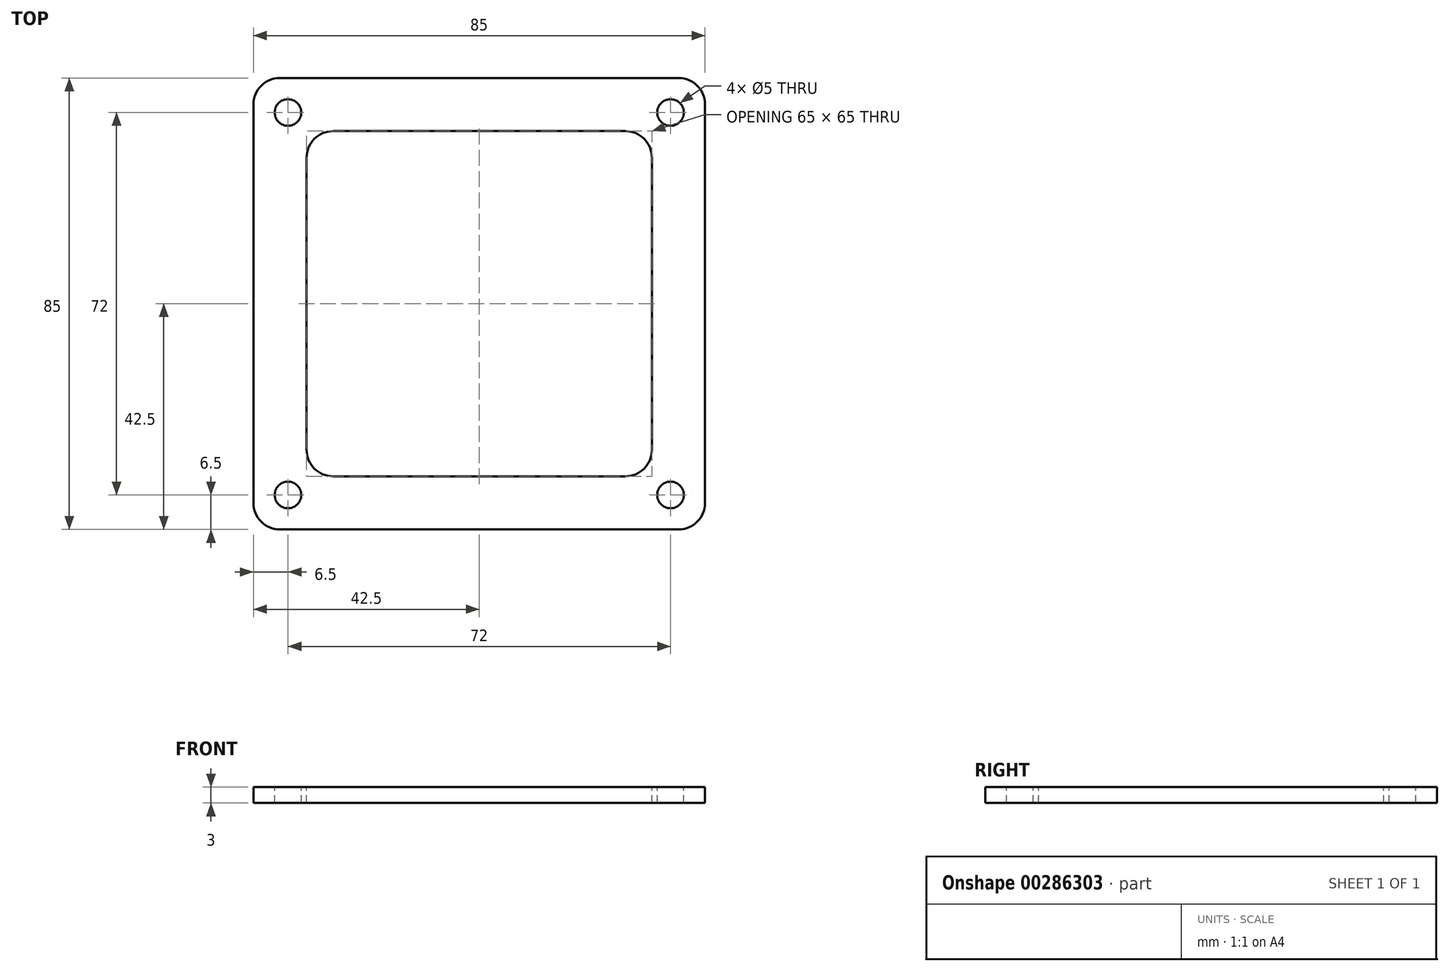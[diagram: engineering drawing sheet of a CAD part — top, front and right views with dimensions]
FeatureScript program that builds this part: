
annotation { "Feature Type Name" : "Feature", "Feature Type Description" : "" }
export const myFeature = defineFeature(function(context is Context, id is Id, definition is map)
    precondition{}
    {
        {
            var Q0;
            Q0=qCreatedBy(makeId("Top.planeOp"),FACE);
            var sketch = newSketch(context, id + "F0", { "sketchPlane" : qUnion([Q0])});
            skLineSegment(sketch, "E0.bottom", {"start": v(5, 0) * mm, "end": v(80, 0) * mm});
            skLineSegment(sketch, "E0.top", {"start": v(5, 85) * mm, "end": v(80, 85) * mm});
            skLineSegment(sketch, "E0.left", {"start": v(0, 5) * mm, "end": v(0, 80) * mm});
            skLineSegment(sketch, "E0.right", {"start": v(85, 5) * mm, "end": v(85, 80) * mm});
            skPoint(sketch, "E1.visualSharp", {"position": v(0, 0) * mm});
            skArc(sketch, "E1.filletArc", {"start": v(0, 5) * mm, "mid": v(1.46, 1.46) * mm, "end": v(5, 0) * mm});
            skPoint(sketch, "E2.visualSharp", {"position": v(0, 85) * mm});
            skArc(sketch, "E2.filletArc", {"start": v(5, 85) * mm, "mid": v(1.46, 83.54) * mm, "end": v(0, 80) * mm});
            skPoint(sketch, "E3.visualSharp", {"position": v(85, 85) * mm});
            skArc(sketch, "E3.filletArc", {"start": v(85, 80) * mm, "mid": v(83.54, 83.54) * mm, "end": v(80, 85) * mm});
            skPoint(sketch, "E4.visualSharp", {"position": v(85, 0) * mm});
            skArc(sketch, "E4.filletArc", {"start": v(80, 0) * mm, "mid": v(83.54, 1.46) * mm, "end": v(85, 5) * mm});
            skSolve(sketch);
        }
        {
            var Q0;
            Q0 = qSketchRegion(id + "F0", true);
            extrude(context, id + "F1", {"entities" : qUnion([Q0]), "depth" : 3 * mm});
        }
        {
            var Q0;
            Q0=makeQuery(id+"F1.opExtrude","CAP_FACE",FACE,{"disambiguationData":[OSD([sQuery(id+"F0.wireOp",EDGE,"E0.bottom"),sQuery(id+"F0.wireOp",EDGE,"E0.top"),sQuery(id+"F0.wireOp",EDGE,"E0.left"),sQuery(id+"F0.wireOp",EDGE,"E0.right")])],"isStart":false});
            var sketch = newSketch(context, id + "F2", { "sketchPlane" : qUnion([Q0])});
            skCircle(sketch, "E5", {"center": v(6.5, 6.5) * mm, "radius": 2.5 * mm});
            skCircle(sketch, "E6.0.1.0", {"center": v(6.5, 78.5) * mm, "radius": 2.5 * mm});
            skCircle(sketch, "E6.1.0.0", {"center": v(78.5, 6.5) * mm, "radius": 2.5 * mm});
            skCircle(sketch, "E6.1.1.0", {"center": v(78.5, 78.5) * mm, "radius": 2.5 * mm});
            skLineSegment(sketch, "E6.direction1", {"start": v(6.5, 6.5) * mm, "end": v(78.5, 6.5) * mm, "construction": true});
            skLineSegment(sketch, "E6.direction2", {"start": v(6.5, 6.5) * mm, "end": v(6.5, 78.5) * mm, "construction": true});
            skLineSegment(sketch, "E7.bottom", {"start": v(15, 75) * mm, "end": v(70, 75) * mm});
            skLineSegment(sketch, "E7.top", {"start": v(15, 10) * mm, "end": v(70, 10) * mm});
            skLineSegment(sketch, "E7.left", {"start": v(10, 70) * mm, "end": v(10, 15) * mm});
            skLineSegment(sketch, "E7.right", {"start": v(75, 70) * mm, "end": v(75, 15) * mm});
            skPoint(sketch, "E8.visualSharp", {"position": v(10, 10) * mm});
            skArc(sketch, "E8.filletArc", {"start": v(10, 15) * mm, "mid": v(11.46, 11.46) * mm, "end": v(15, 10) * mm});
            skPoint(sketch, "E9.visualSharp", {"position": v(75, 10) * mm});
            skArc(sketch, "E9.filletArc", {"start": v(70, 10) * mm, "mid": v(73.54, 11.46) * mm, "end": v(75, 15) * mm});
            skPoint(sketch, "E10.visualSharp", {"position": v(75, 75) * mm});
            skArc(sketch, "E10.filletArc", {"start": v(75, 70) * mm, "mid": v(73.54, 73.54) * mm, "end": v(70, 75) * mm});
            skPoint(sketch, "E11.visualSharp", {"position": v(10, 75) * mm});
            skArc(sketch, "E11.filletArc", {"start": v(15, 75) * mm, "mid": v(11.46, 73.54) * mm, "end": v(10, 70) * mm});
            skSolve(sketch);
        }
        {
            var Q0;
            Q0 = qSketchRegion(id + "F2", true);
            extrude(context, id + "F3", {"entities" : qUnion([Q0]), "operationType" : NewBodyOperationType.REMOVE, "endBound" : BoundingType.THROUGH_ALL, "oppositeDirection" : true, "depth" : 25 * mm});
        }
    });
